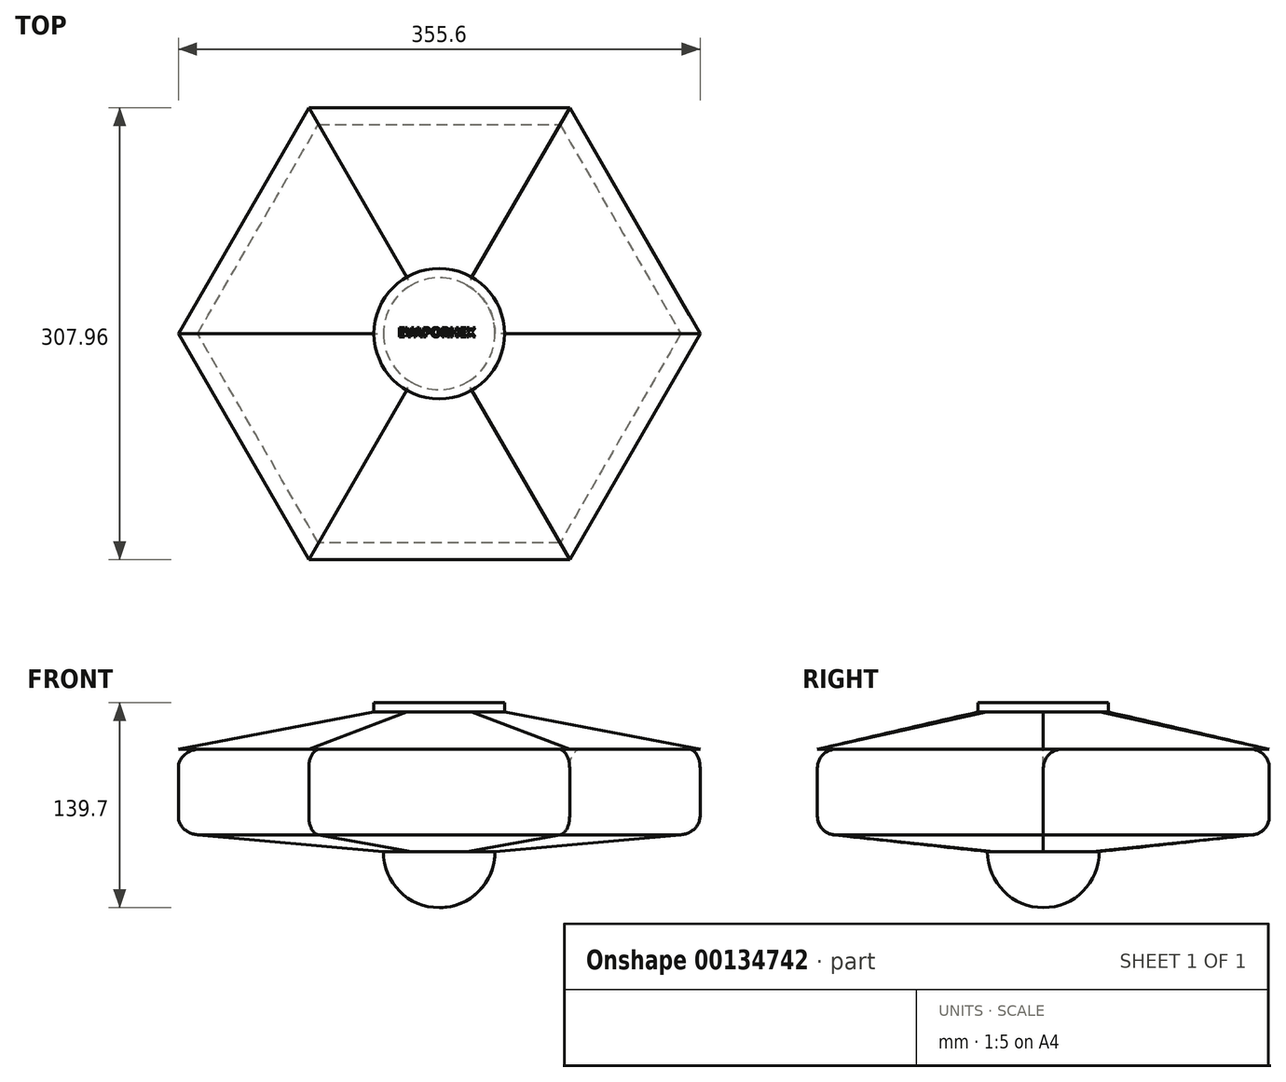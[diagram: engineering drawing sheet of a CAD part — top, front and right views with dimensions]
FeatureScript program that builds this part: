
annotation { "Feature Type Name" : "Feature", "Feature Type Description" : "" }
export const myFeature = defineFeature(function(context is Context, id is Id, definition is map)
    precondition{}
    {
        {
            var Q0;
            Q0=qCreatedBy(makeId("Top.planeOp"),FACE);
            var sketch = newSketch(context, id + "F0", { "sketchPlane" : qUnion([Q0])});
            skCircle(sketch, "E0.cCircle", {"center": v(0, 0) * mm, "radius": 153.98 * mm, "construction": true});
            skLineSegment(sketch, "E0.0", {"start": v(-88.9, 153.98) * mm, "end": v(88.9, 153.98) * mm});
            skLineSegment(sketch, "E0.1", {"start": v(88.9, 153.98) * mm, "end": v(177.8, 0) * mm});
            skLineSegment(sketch, "E0.2", {"start": v(177.8, 0) * mm, "end": v(88.9, -153.98) * mm});
            skLineSegment(sketch, "E0.3", {"start": v(88.9, -153.98) * mm, "end": v(-88.9, -153.98) * mm});
            skLineSegment(sketch, "E0.4", {"start": v(-88.9, -153.98) * mm, "end": v(-177.8, 0) * mm});
            skLineSegment(sketch, "E0.5", {"start": v(-177.8, 0) * mm, "end": v(-88.9, 153.98) * mm});
            skPoint(sketch, "E0.0.midPoint", {"position": v(0, 153.98) * mm});
            skSolve(sketch);
        }
        {
            var Q0;
            Q0 = qSketchRegion(id + "F0", true);
            extrude(context, id + "F1", {"entities" : qUnion([Q0]), "depth" : 57.15 * mm});
        }
        {
            var Q0;
            Q0=makeQuery(id+"F1.opExtrude","CAP_FACE",FACE,{"disambiguationData":[OSD([sQuery(id+"F0.wireOp",EDGE,"E0.0"),sQuery(id+"F0.wireOp",EDGE,"E0.1"),sQuery(id+"F0.wireOp",EDGE,"E0.2"),sQuery(id+"F0.wireOp",EDGE,"E0.3"),sQuery(id+"F0.wireOp",EDGE,"E0.4"),sQuery(id+"F0.wireOp",EDGE,"E0.5")])],"isStart":false});
            cPlane(context, id + "F2", {"entities" : qUnion([Q0]), "cplaneType" : CPlaneType.OFFSET, "offset" : 25.4 * mm, "width" : 152.4 * mm, "height" : 152.4 * mm});
        }
        {
            var Q0;
            Q0=qCreatedBy(id+"F2.planeOp",FACE);
            var sketch = newSketch(context, id + "F3", { "sketchPlane" : qUnion([Q0])});
            skCircle(sketch, "E1", {"center": v(0, 0) * mm, "radius": 44.45 * mm});
            skSolve(sketch);
        }
        {
            var Q0;
            Q0 = qSketchRegion(id + "F3", true);
            extrude(context, id + "F4", {"entities" : qUnion([Q0]), "depth" : 6.35 * mm});
        }
        {
            var Q0;
            Q0=makeQuery(id+"F1.opExtrude","CAP_FACE",FACE,{"disambiguationData":[OSD([sQuery(id+"F0.wireOp",EDGE,"E0.0"),sQuery(id+"F0.wireOp",EDGE,"E0.1"),sQuery(id+"F0.wireOp",EDGE,"E0.2"),sQuery(id+"F0.wireOp",EDGE,"E0.3"),sQuery(id+"F0.wireOp",EDGE,"E0.4"),sQuery(id+"F0.wireOp",EDGE,"E0.5")])],"isStart":false});
            var Q1;
            Q1=makeQuery(id+"F4.opExtrude","CAP_FACE",FACE,{"disambiguationData":[OSD([sQuery(id+"F3.wireOp",EDGE,"E1")])],"isStart":true});
            loft(context, id + "F5", {"sheetProfilesArray" : [{ "sheetProfileEntities" : qUnion([Q0]) }, { "sheetProfileEntities" : qUnion([Q1]) }]});
        }
        {
            var Q0;
            Q0=makeQuery(id+"F1.opExtrude","CAP_FACE",FACE,{"disambiguationData":[OSD([sQuery(id+"F0.wireOp",EDGE,"E0.0"),sQuery(id+"F0.wireOp",EDGE,"E0.1"),sQuery(id+"F0.wireOp",EDGE,"E0.2"),sQuery(id+"F0.wireOp",EDGE,"E0.3"),sQuery(id+"F0.wireOp",EDGE,"E0.4"),sQuery(id+"F0.wireOp",EDGE,"E0.5")])],"isStart":true});
            cPlane(context, id + "F6", {"entities" : qUnion([Q0]), "cplaneType" : CPlaneType.OFFSET, "offset" : 12.7 * mm, "width" : 152.4 * mm, "height" : 152.4 * mm});
        }
        {
            var Q0;
            Q0=qCreatedBy(makeId("Front.planeOp"),FACE);
            var sketch = newSketch(context, id + "F7", { "sketchPlane" : qUnion([Q0])});
            skLineSegment(sketch, "E2", {"start": v(0, 0) * mm, "end": v(0, -74.11) * mm, "construction": true});
            skArc(sketch, "E3", {"start": v(0, -50.8) * mm, "mid": v(26.94, -39.64) * mm, "end": v(38.1, -12.7) * mm});
            skLineSegment(sketch, "E4", {"start": v(38.1, -12.7) * mm, "end": v(0, -12.7) * mm});
            skLineSegment(sketch, "E5", {"start": v(0, -50.8) * mm, "end": v(0, -12.7) * mm});
            skSolve(sketch);
        }
        {
            var Q0;
            Q0 = qSketchRegion(id + "F7", true);
            var Q1;
            Q1=sQuery(id+"F7.wireOp",EDGE,"E2");
            revolve(context, id + "F8", {"entities" : qUnion([Q0]), "axis" : qUnion([Q1]), "revolveType" : RevolveType.FULL});
        }
        {
            var Q1;
            Q1=makeQuery(id+"F1.opExtrude","CAP_FACE",FACE,{"disambiguationData":[OSD([sQuery(id+"F0.wireOp",EDGE,"E0.0"),sQuery(id+"F0.wireOp",EDGE,"E0.1"),sQuery(id+"F0.wireOp",EDGE,"E0.2"),sQuery(id+"F0.wireOp",EDGE,"E0.3"),sQuery(id+"F0.wireOp",EDGE,"E0.4"),sQuery(id+"F0.wireOp",EDGE,"E0.5")])],"isStart":true});
            var Q2;
            Q2=makeQuery(id+"F8.opRevolve","SWEPT_FACE",FACE,{"disambiguationData":[OSD([sQuery(id+"F7.wireOp",EDGE,"E4")])]});
            loft(context, id + "F9", {"operationType" : NewBodyOperationType.ADD, "sheetProfilesArray" : [{ "sheetProfileEntities" : qUnion([Q1]) }, { "sheetProfileEntities" : qUnion([Q2]) }]});
        }
        {
            var Q0;
            Q0=makeQuery(id+"F4.opExtrude","CAP_FACE",FACE,{"disambiguationData":[OSD([sQuery(id+"F3.wireOp",EDGE,"E1")])],"isStart":false});
            var sketch = newSketch(context, id + "F10", { "sketchPlane" : qUnion([Q0])});
            skText(sketch, "E6", { "text": "EVAPORHEX", "fontName": "OpenSans-Bold.ttf"});
            const initialGuessF10  = {"E6": [-0.02807, -0.00215, 1, 0, 0.00635]};
            skSetInitialGuess(sketch, initialGuessF10);
            skSolve(sketch);
        }
        {
            var Q0;
            Q0 = qSketchRegion(id + "F10", true);
            extrude(context, id + "F11", {"entities" : qUnion([Q0]), "operationType" : NewBodyOperationType.REMOVE, "oppositeDirection" : true, "depth" : 0.25 * mm});
        }
        {
            var Q0;
            Q0=makeQuery(id+"F1.opExtrude","CAP_EDGE",EDGE,{"disambiguationData":[OSD([sQuery(id+"F0.wireOp",EDGE,"E0.4")])],"isStart":false});
            var Q1;
            Q1=makeQuery(id+"F1.opExtrude","CAP_EDGE",EDGE,{"disambiguationData":[OSD([sQuery(id+"F0.wireOp",EDGE,"E0.2")])],"isStart":false});
            var Q2;
            Q2=makeQuery(id+"F1.opExtrude","CAP_EDGE",EDGE,{"disambiguationData":[OSD([sQuery(id+"F0.wireOp",EDGE,"E0.3")])],"isStart":false});
            var Q3;
            Q3=makeQuery(id+"F1.opExtrude","CAP_EDGE",EDGE,{"disambiguationData":[OSD([sQuery(id+"F0.wireOp",EDGE,"E0.0")])],"isStart":false});
            var Q4;
            Q4=makeQuery(id+"F1.opExtrude","CAP_EDGE",EDGE,{"disambiguationData":[OSD([sQuery(id+"F0.wireOp",EDGE,"E0.5")])],"isStart":false});
            var Q5;
            {var subQ0=sQuery(id+"F0.wireOp",EDGE,"E0.3");Q5=makeQuery(id+"F9.boolean.opBoolean","MERGE",EDGE,{"derivedFrom":[makeQuery(id+"F1.opExtrude","CAP_EDGE",EDGE,{"disambiguationData":[OSD([subQ0])],"isStart":true}),makeQuery(id+"F9.opLoft","MID_CAP_EDGE",EDGE,{"disambiguationData":[OSD([sQuery(id+"F0.wireOp",EDGE,"E0.2"),subQ0,sQuery(id+"F0.wireOp",EDGE,"E0.4")])],"capPos":0.0})]});}
            var Q6;
            {var subQ0=sQuery(id+"F0.wireOp",EDGE,"E0.4");Q6=makeQuery(id+"F9.boolean.opBoolean","MERGE",EDGE,{"derivedFrom":[makeQuery(id+"F1.opExtrude","CAP_EDGE",EDGE,{"disambiguationData":[OSD([subQ0])],"isStart":true}),makeQuery(id+"F9.opLoft","MID_CAP_EDGE",EDGE,{"disambiguationData":[OSD([sQuery(id+"F0.wireOp",EDGE,"E0.3"),subQ0,sQuery(id+"F0.wireOp",EDGE,"E0.5")])],"capPos":0.0})]});}
            var Q7;
            {var subQ0=sQuery(id+"F0.wireOp",EDGE,"E0.2");Q7=makeQuery(id+"F9.boolean.opBoolean","MERGE",EDGE,{"derivedFrom":[makeQuery(id+"F1.opExtrude","CAP_EDGE",EDGE,{"disambiguationData":[OSD([subQ0])],"isStart":true}),makeQuery(id+"F9.opLoft","MID_CAP_EDGE",EDGE,{"disambiguationData":[OSD([sQuery(id+"F0.wireOp",EDGE,"E0.1"),subQ0,sQuery(id+"F0.wireOp",EDGE,"E0.3")])],"capPos":0.0})]});}
            var Q8;
            {var subQ0=sQuery(id+"F0.wireOp",EDGE,"E0.1");Q8=makeQuery(id+"F9.boolean.opBoolean","MERGE",EDGE,{"derivedFrom":[makeQuery(id+"F1.opExtrude","CAP_EDGE",EDGE,{"disambiguationData":[OSD([subQ0])],"isStart":true}),makeQuery(id+"F9.opLoft","MID_CAP_EDGE",EDGE,{"disambiguationData":[OSD([sQuery(id+"F0.wireOp",EDGE,"E0.0"),subQ0,sQuery(id+"F0.wireOp",EDGE,"E0.2")])],"capPos":0.0})]});}
            var Q9;
            {var subQ0=sQuery(id+"F0.wireOp",EDGE,"E0.0");Q9=makeQuery(id+"F9.boolean.opBoolean","MERGE",EDGE,{"derivedFrom":[makeQuery(id+"F1.opExtrude","CAP_EDGE",EDGE,{"disambiguationData":[OSD([subQ0])],"isStart":true}),makeQuery(id+"F9.opLoft","MID_CAP_EDGE",EDGE,{"disambiguationData":[OSD([subQ0,sQuery(id+"F0.wireOp",EDGE,"E0.1"),sQuery(id+"F0.wireOp",EDGE,"E0.5")])],"capPos":0.0})]});}
            var Q10;
            {var subQ0=sQuery(id+"F0.wireOp",EDGE,"E0.5");Q10=makeQuery(id+"F9.boolean.opBoolean","MERGE",EDGE,{"derivedFrom":[makeQuery(id+"F1.opExtrude","CAP_EDGE",EDGE,{"disambiguationData":[OSD([subQ0])],"isStart":true}),makeQuery(id+"F9.opLoft","MID_CAP_EDGE",EDGE,{"disambiguationData":[OSD([sQuery(id+"F0.wireOp",EDGE,"E0.0"),sQuery(id+"F0.wireOp",EDGE,"E0.4"),subQ0])],"capPos":0.0})]});}
            fillet(context, id + "F12", {"entities" : qUnion([Q0, Q1, Q2, Q3, Q4, Q5, Q6, Q7, Q8, Q9, Q10]), "radius" : 12.7 * mm, "tangentPropagation" : true, "allowEdgeOverflow" : false});
        }
    });
